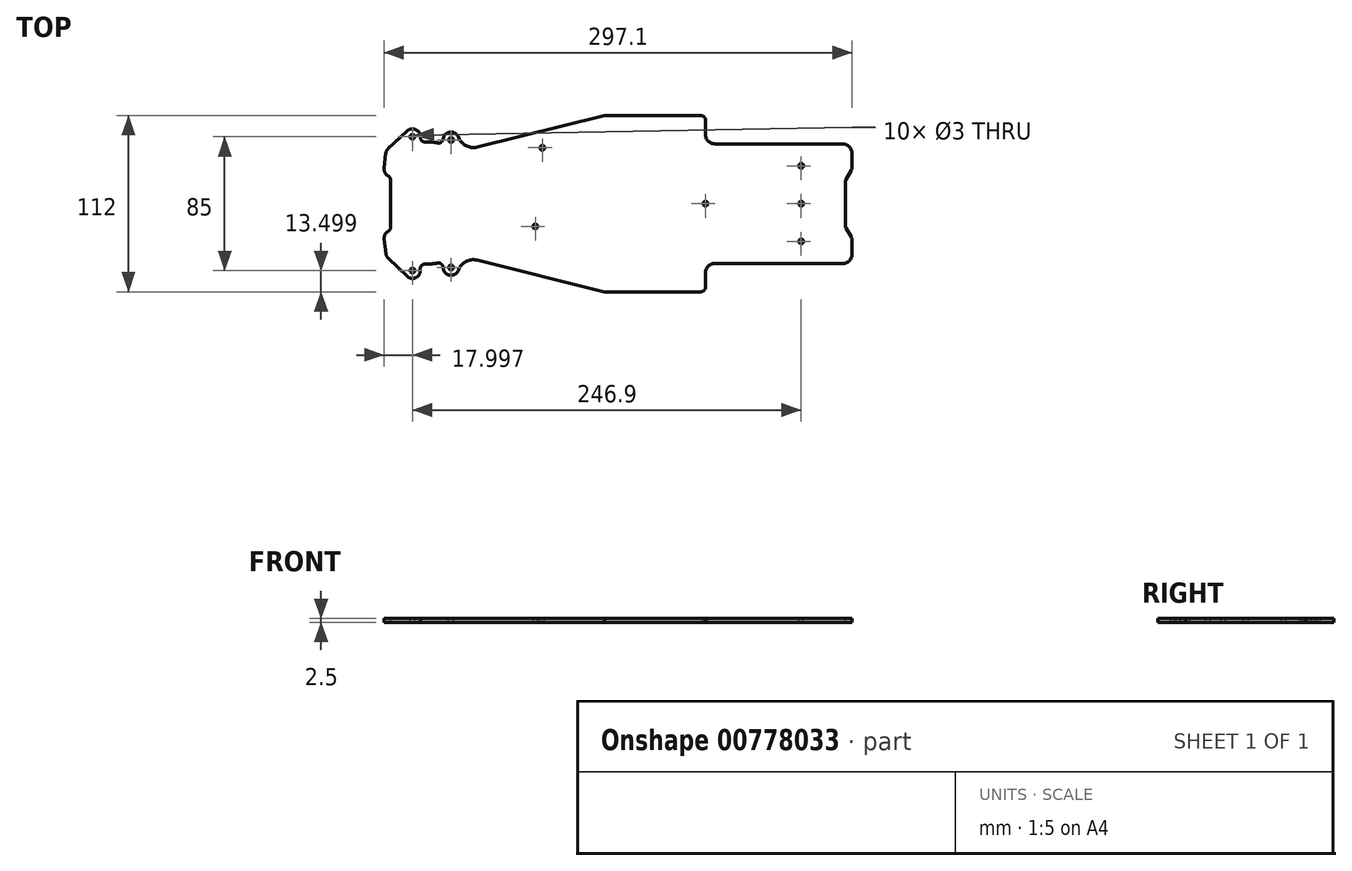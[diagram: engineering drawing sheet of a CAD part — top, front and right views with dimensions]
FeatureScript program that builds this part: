
annotation { "Feature Type Name" : "Feature", "Feature Type Description" : "" }
export const myFeature = defineFeature(function(context is Context, id is Id, definition is map)
    precondition{}
    {
        {
            var Q0;
            Q0=qCreatedBy(makeId("Top.planeOp"),FACE);
            var sketch = newSketch(context, id + "F0", { "sketchPlane" : qUnion([Q0])});
            skLineSegment(sketch, "E0", {"start": v(142.55, 20.93) * mm, "end": v(61.55, 20.93) * mm});
            skLineSegment(sketch, "E1", {"start": v(142.55, -55.07) * mm, "end": v(61.55, -55.07) * mm});
            skLineSegment(sketch, "E2", {"start": v(148.55, 14.93) * mm, "end": v(148.55, 5.73) * mm});
            skArc(sketch, "E3", {"start": v(148.55, 14.93) * mm, "mid": v(146.8, 19.17) * mm, "end": v(142.55, 20.93) * mm});
            skCircle(sketch, "E4", {"center": v(55.55, -17.07) * mm, "radius": 1.5 * mm});
            skCircle(sketch, "E5", {"center": v(116.35, 6.93) * mm, "radius": 1.5 * mm});
            skCircle(sketch, "E6", {"center": v(116.35, -41.07) * mm, "radius": 1.5 * mm});
            skCircle(sketch, "E7", {"center": v(116.35, -17.07) * mm, "radius": 1.5 * mm});
            skLineSegment(sketch, "E8", {"start": v(55.55, 35.93) * mm, "end": v(55.55, 26.93) * mm});
            skArc(sketch, "E9", {"start": v(55.55, 35.93) * mm, "mid": v(54.67, 38.05) * mm, "end": v(52.55, 38.93) * mm});
            skArc(sketch, "E10", {"start": v(52.55, -73.07) * mm, "mid": v(54.67, -72.2) * mm, "end": v(55.55, -70.07) * mm});
            skLineSegment(sketch, "E11", {"start": v(55.55, -61.07) * mm, "end": v(55.55, -70.07) * mm});
            skArc(sketch, "E12", {"start": v(55.55, 26.93) * mm, "mid": v(57.3, 22.69) * mm, "end": v(61.55, 20.93) * mm});
            skArc(sketch, "E13", {"start": v(61.55, -55.07) * mm, "mid": v(57.3, -56.83) * mm, "end": v(55.55, -61.07) * mm});
            skLineSegment(sketch, "E14", {"start": v(148.55, -39.87) * mm, "end": v(148.55, -49.07) * mm});
            skArc(sketch, "E15", {"start": v(142.55, -55.07) * mm, "mid": v(146.8, -53.31) * mm, "end": v(148.55, -49.07) * mm});
            skLineSegment(sketch, "E16", {"start": v(148.16, 4.24) * mm, "end": v(144.75, -1.73) * mm});
            skLineSegment(sketch, "E17", {"start": v(144.75, -32.42) * mm, "end": v(148.16, -38.38) * mm});
            skArc(sketch, "E18", {"start": v(144.75, -1.73) * mm, "mid": v(144.6, -2.08) * mm, "end": v(144.55, -2.47) * mm});
            skArc(sketch, "E19", {"start": v(144.55, -31.67) * mm, "mid": v(144.6, -32.06) * mm, "end": v(144.75, -32.42) * mm});
            skArc(sketch, "E20", {"start": v(148.16, 4.24) * mm, "mid": v(148.45, 4.96) * mm, "end": v(148.55, 5.73) * mm});
            skArc(sketch, "E21", {"start": v(148.55, -39.87) * mm, "mid": v(148.45, -39.1) * mm, "end": v(148.16, -38.38) * mm});
            skLineSegment(sketch, "E22", {"start": v(-8.45, -73.07) * mm, "end": v(52.55, -73.07) * mm});
            skCircle(sketch, "E23", {"center": v(-130.55, 25.43) * mm, "radius": 1.5 * mm});
            skCircle(sketch, "E24", {"center": v(-130.55, -59.57) * mm, "radius": 1.5 * mm});
            skCircle(sketch, "E25", {"center": v(-106.05, 23.43) * mm, "radius": 1.5 * mm});
            skCircle(sketch, "E26", {"center": v(-106.05, -57.57) * mm, "radius": 1.5 * mm});
            skArc(sketch, "E27", {"start": v(-122.56, -55.46) * mm, "mid": v(-118.57, -55.34) * mm, "end": v(-114.6, -54.81) * mm});
            skArc(sketch, "E28", {"start": v(-122.56, -55.46) * mm, "mid": v(-124.87, -56.47) * mm, "end": v(-125.6, -58.88) * mm});
            skArc(sketch, "E29", {"start": v(-111.05, -57.7) * mm, "mid": v(-106.86, -62.5) * mm, "end": v(-101.36, -59.28) * mm});
            skArc(sketch, "E30", {"start": v(-111.05, -57.7) * mm, "mid": v(-112.16, -55.43) * mm, "end": v(-114.6, -54.81) * mm});
            skArc(sketch, "E31", {"start": v(-114.7, 21.46) * mm, "mid": v(-118.5, 22.07) * mm, "end": v(-122.34, 22.09) * mm});
            skArc(sketch, "E32", {"start": v(-101.36, 25.14) * mm, "mid": v(-106.63, 28.4) * mm, "end": v(-111.02, 24.02) * mm});
            skArc(sketch, "E33", {"start": v(-125.56, 25.21) * mm, "mid": v(-128.47, 29.97) * mm, "end": v(-133.97, 29.08) * mm});
            skArc(sketch, "E34", {"start": v(-125.56, 25.21) * mm, "mid": v(-124.65, 22.93) * mm, "end": v(-122.34, 22.09) * mm});
            skArc(sketch, "E35", {"start": v(-114.7, 21.46) * mm, "mid": v(-112.28, 21.92) * mm, "end": v(-111.02, 24.02) * mm});
            skLineSegment(sketch, "E36", {"start": v(-133.97, 29.08) * mm, "end": v(-145.97, 17.83) * mm});
            skLineSegment(sketch, "E37", {"start": v(-145.89, -51.8) * mm, "end": v(-134.01, -63.18) * mm});
            skArc(sketch, "E38", {"start": v(-147.33, -48.93) * mm, "mid": v(-146.86, -50.5) * mm, "end": v(-145.89, -51.8) * mm});
            skLineSegment(sketch, "E39", {"start": v(-147.52, 14.72) * mm, "end": v(-148.52, 5.47) * mm});
            skArc(sketch, "E40", {"start": v(-145.97, 17.83) * mm, "mid": v(-147.03, 16.41) * mm, "end": v(-147.52, 14.72) * mm});
            skLineSegment(sketch, "E41", {"start": v(-148.51, -39.7) * mm, "end": v(-147.33, -48.93) * mm});
            skLineSegment(sketch, "E42", {"start": v(-144.52, -2.02) * mm, "end": v(-144.52, -32.13) * mm});
            skArc(sketch, "E43", {"start": v(-148.52, 5.47) * mm, "mid": v(-148, 2.66) * mm, "end": v(-146.03, 0.59) * mm});
            skArc(sketch, "E44", {"start": v(-146.03, -34.73) * mm, "mid": v(-148.03, -36.84) * mm, "end": v(-148.51, -39.7) * mm});
            skArc(sketch, "E45", {"start": v(-146.03, -34.73) * mm, "mid": v(-144.93, -33.63) * mm, "end": v(-144.52, -32.13) * mm});
            skArc(sketch, "E46", {"start": v(-144.52, -2.02) * mm, "mid": v(-144.93, -0.51) * mm, "end": v(-146.03, 0.59) * mm});
            skCircle(sketch, "E47", {"center": v(-48.05, 18.43) * mm, "radius": 1.5 * mm});
            skCircle(sketch, "E48", {"center": v(-52.55, -31.57) * mm, "radius": 1.5 * mm});
            skArc(sketch, "E49", {"start": v(-89.56, 18.86) * mm, "mid": v(-89.49, 18.88) * mm, "end": v(-89.41, 18.9) * mm});
            skArc(sketch, "E50", {"start": v(-89.41, -53.04) * mm, "mid": v(-89.49, -53.02) * mm, "end": v(-89.56, -53) * mm});
            skLineSegment(sketch, "E51", {"start": v(-8.45, 38.93) * mm, "end": v(-89.56, 18.86) * mm});
            skLineSegment(sketch, "E52", {"start": v(-8.45, -73.07) * mm, "end": v(-89.56, -53) * mm});
            skArc(sketch, "E53", {"start": v(-101.36, 25.14) * mm, "mid": v(-96.66, 19.74) * mm, "end": v(-89.56, 18.86) * mm});
            skArc(sketch, "E54", {"start": v(-89.56, -53) * mm, "mid": v(-96.66, -53.88) * mm, "end": v(-101.36, -59.28) * mm});
            skLineSegment(sketch, "E55", {"start": v(52.55, 38.93) * mm, "end": v(-8.45, 38.93) * mm});
            skLineSegment(sketch, "E56", {"start": v(144.55, -2.47) * mm, "end": v(144.55, -31.67) * mm});
            skArc(sketch, "E57", {"start": v(-134.01, -63.18) * mm, "mid": v(-128.28, -64.02) * mm, "end": v(-125.6, -58.88) * mm});
            skLineSegment(sketch, "E58", {"start": v(-99.05, 40.39) * mm, "end": v(-99.05, -79.75) * mm, "construction": true});
            skLineSegment(sketch, "E59", {"start": v(108.95, 40.39) * mm, "end": v(108.95, -79.75) * mm, "construction": true});
            skLineSegment(sketch, "E60", {"start": v(190.88, -17.07) * mm, "end": v(-177.29, -17.07) * mm, "construction": true});
            skSolve(sketch);
        }
        {
            var Q0;
            Q0=makeQuery(id+"F0.imprint","IMPRINT",FACE,{"disambiguationData":[TD([[makeQuery(id+"F0.imprint","IMPRINT",EDGE,{"derivedFrom":sQuery(id+"F0.wireOp",EDGE,"E0")}),1.0]])]});
            extrude(context, id + "F1", {"entities" : qUnion([Q0]), "oppositeDirection" : true, "depth" : 2.5 * mm, "offsetDistance" : 25 * mm});
        }
    });
